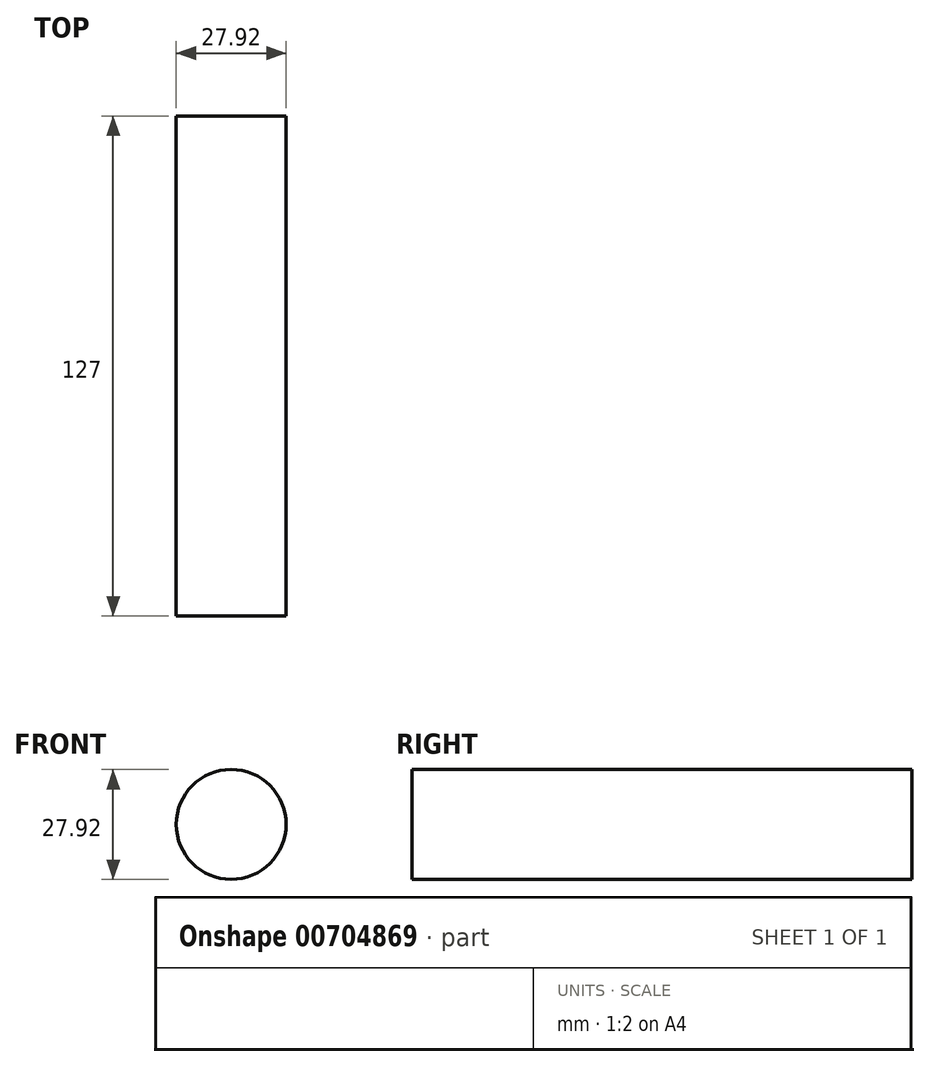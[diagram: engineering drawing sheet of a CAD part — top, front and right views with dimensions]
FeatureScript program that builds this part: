
annotation { "Feature Type Name" : "Feature", "Feature Type Description" : "" }
export const myFeature = defineFeature(function(context is Context, id is Id, definition is map)
    precondition{}
    {
        {
            var Q0;
            Q0=qCreatedBy(makeId("Front.planeOp"),FACE);
            var sketch = newSketch(context, id + "F0", { "sketchPlane" : qUnion([Q0])});
            skCircle(sketch, "E0", {"center": v(0, 0) * mm, "radius": 13.96 * mm});
            skSolve(sketch);
        }
        {
            var Q0;
            Q0=makeQuery(id+"F0.imprint","IMPRINT",FACE,{"disambiguationData":[TD([[makeQuery(id+"F0.imprint","IMPRINT",EDGE,{"derivedFrom":sQuery(id+"F0.wireOp",EDGE,"E0")}),1.0]])]});
            extrude(context, id + "F1", {"entities" : qUnion([Q0]), "depth" : 127 * mm, "offsetDistance" : 25.4 * mm});
        }
        {
            var Q0;
            Q0=makeQuery(id+"F1.opExtrude","CAP_FACE",FACE,{"disambiguationData":[OSD([sQuery(id+"F0.wireOp",EDGE,"E0")])],"isStart":false});
            var sketch = newSketch(context, id + "F2", { "sketchPlane" : qUnion([Q0])});
            skCircle(sketch, "E1", {"center": v(0, 0) * mm, "radius": 3.47 * mm});
            skSolve(sketch);
        }
        {
            var Q0;
            Q0=sQuery(id+"F2.wireOp",EDGE,"E1");
            extrude(context, id + "F3", {"bodyType" : ToolBodyType.SURFACE, "surfaceEntities" : qUnion([Q0]), "depth" : 50.8 * mm, "offsetDistance" : 25.4 * mm});
        }
        {
            var Q0;
            Q0=makeQuery(id+"F1.opExtrude","CAP_FACE",FACE,{"disambiguationData":[OSD([sQuery(id+"F0.wireOp",EDGE,"E0")])],"isStart":true});
            var sketch = newSketch(context, id + "F4", { "sketchPlane" : qUnion([Q0])});
            skSolve(sketch);
        }
        {
            var Q0;
            Q0=makeQuery(id+"F4.imprint","IMPRINT",FACE,{"disambiguationData":[TD([[makeQuery(id+"F4.imprint","IMPRINT",EDGE,{"derivedFrom":makeQuery(id+"F1.opExtrude","CAP_EDGE",EDGE,{"disambiguationData":[OSD([sQuery(id+"F0.wireOp",EDGE,"E0")])],"isStart":true})}),-1.0]])]});
            var sketch = newSketch(context, id + "F5", { "sketchPlane" : qUnion([Q0])});
            skCircle(sketch, "E2", {"center": v(0, 0) * mm, "radius": 3.81 * mm});
            skSolve(sketch);
        }
        {
            var Q0;
            Q0=sQuery(id+"F5.wireOp",EDGE,"E2");
            extrude(context, id + "F6", {"bodyType" : ToolBodyType.SURFACE, "surfaceEntities" : qUnion([Q0]), "depth" : 50.8 * mm, "offsetDistance" : 25.4 * mm});
        }
    });
